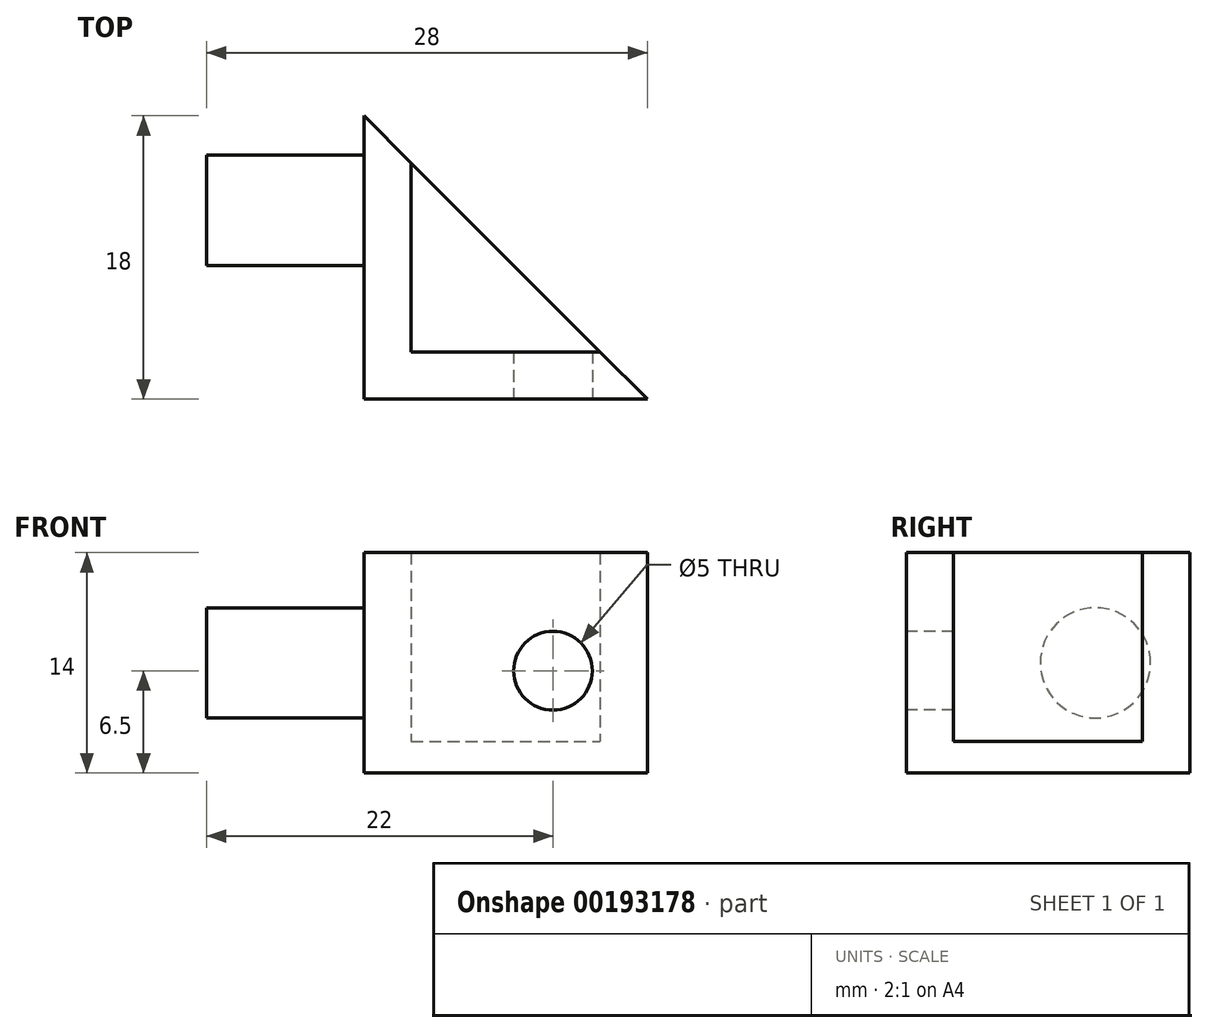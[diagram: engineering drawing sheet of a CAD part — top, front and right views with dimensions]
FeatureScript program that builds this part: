
annotation { "Feature Type Name" : "Feature", "Feature Type Description" : "" }
export const myFeature = defineFeature(function(context is Context, id is Id, definition is map)
    precondition{}
    {
        {
            var Q0;
            Q0=qCreatedBy(makeId("Top.planeOp"),FACE);
            var sketch = newSketch(context, id + "F0", { "sketchPlane" : qUnion([Q0])});
            skLineSegment(sketch, "E0", {"start": v(0, 0) * mm, "end": v(0, 18) * mm});
            skLineSegment(sketch, "E1", {"start": v(0, 18) * mm, "end": v(18, 0) * mm});
            skLineSegment(sketch, "E2", {"start": v(18, 0) * mm, "end": v(0, 0) * mm});
            skSolve(sketch);
        }
        {
            var Q0;
            Q0 = qSketchRegion(id + "F0", true);
            extrude(context, id + "F1", {"entities" : qUnion([Q0]), "depth" : 2 * mm});
        }
        {
            var Q0;
            Q0=makeQuery(id+"F1.opExtrude","CAP_FACE",FACE,{"disambiguationData":[OSD([sQuery(id+"F0.wireOp",EDGE,"E0"),sQuery(id+"F0.wireOp",EDGE,"E1"),sQuery(id+"F0.wireOp",EDGE,"E2")])],"isStart":false});
            var sketch = newSketch(context, id + "F2", { "sketchPlane" : qUnion([Q0])});
            skLineSegment(sketch, "E3", {"start": v(0, 0) * mm, "end": v(0, 18) * mm});
            skLineSegment(sketch, "E4", {"start": v(0, 18) * mm, "end": v(3, 15) * mm});
            skLineSegment(sketch, "E5", {"start": v(3, 15) * mm, "end": v(3, 3) * mm});
            skLineSegment(sketch, "E6", {"start": v(3, 3) * mm, "end": v(15, 3) * mm});
            skLineSegment(sketch, "E7", {"start": v(15, 3) * mm, "end": v(18, 0) * mm});
            skLineSegment(sketch, "E8", {"start": v(18, 0) * mm, "end": v(0, 0) * mm});
            skSolve(sketch);
        }
        {
            var Q0;
            Q0 = qSketchRegion(id + "F2", true);
            extrude(context, id + "F3", {"entities" : qUnion([Q0]), "operationType" : NewBodyOperationType.ADD, "depth" : 12 * mm});
        }
        {
            var Q0;
            Q0=makeQuery(id+"F3.boolean.opBoolean","MERGE",FACE,{"derivedFrom":[makeQuery(id+"F1.opExtrude","SWEPT_FACE",FACE,{"disambiguationData":[OSD([sQuery(id+"F0.wireOp",EDGE,"E0")])]}),makeQuery(id+"F3.opExtrude","SWEPT_FACE",FACE,{"disambiguationData":[OSD([sQuery(id+"F2.wireOp",EDGE,"E3")])]})]});
            var sketch = newSketch(context, id + "F4", { "sketchPlane" : qUnion([Q0])});
            skCircle(sketch, "E9", {"center": v(-12, 7) * mm, "radius": 3.5 * mm});
            skLineSegment(sketch, "E10", {"start": v(-18, 7) * mm, "end": v(0, 7) * mm, "construction": true});
            skSolve(sketch);
        }
        {
            var Q0;
            Q0 = qSketchRegion(id + "F4", true);
            extrude(context, id + "F5", {"entities" : qUnion([Q0]), "operationType" : NewBodyOperationType.ADD, "depth" : 10 * mm});
        }
        {
            var Q0;
            Q0=makeQuery(id+"F3.boolean.opBoolean","MERGE",FACE,{"derivedFrom":[makeQuery(id+"F1.opExtrude","SWEPT_FACE",FACE,{"disambiguationData":[OSD([sQuery(id+"F0.wireOp",EDGE,"E2")])]}),makeQuery(id+"F3.opExtrude","SWEPT_FACE",FACE,{"disambiguationData":[OSD([sQuery(id+"F2.wireOp",EDGE,"E8")])]})]});
            var sketch = newSketch(context, id + "F6", { "sketchPlane" : qUnion([Q0])});
            skCircle(sketch, "E11", {"center": v(12, 6.5) * mm, "radius": 2.5 * mm});
            skLineSegment(sketch, "E12", {"start": v(0, 7) * mm, "end": v(18, 7) * mm, "construction": true});
            skSolve(sketch);
        }
        {
            var Q0;
            Q0 = qSketchRegion(id + "F6", true);
            extrude(context, id + "F7", {"entities" : qUnion([Q0]), "operationType" : NewBodyOperationType.REMOVE, "endBound" : BoundingType.THROUGH_ALL, "oppositeDirection" : true, "depth" : 25 * mm});
        }
    });
